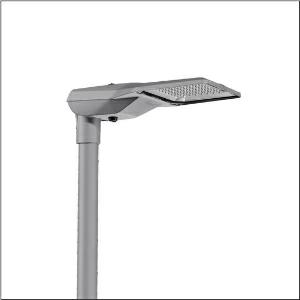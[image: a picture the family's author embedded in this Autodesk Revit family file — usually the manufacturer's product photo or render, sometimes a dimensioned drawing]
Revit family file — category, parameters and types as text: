
# Revit family: streetlight_sl_21_iq_midi___st1_0a_5xe3d31y08nb_4ee3
name_source: partatom
category: Lighting Fixtures
units: mm (PartAtom-declared; Revit-internal decimal feet)

## family parameters
Cut with Voids When Loaded = No
Host = Face
Light Source = No
Part Type = Normal
Room Calculation Point = No
Round Connector Dimension = Use Diameter
Shared = No

## types (1)
- --- (1 x LED, 21550 lm, 136.6 W, 3000K)
    Apparent Load = 137 VA
    CIE Flux Codes = 40 73 97 100 100
    Color Rendering = 70
    Color Temperature = 3000K
    Default Elevation = 1800 mm
    Description = Streetlight SL 21 iQ midi, mast luminaire, primary light control with lens, of PMMA, primary optical cover: cover, of toughened safety glass, transparent, light distribution: ST1.0a, light emission: direct distribution, primary light characteristic: asymmetric, installation type: post-top, side-entry, LED, High Power LED, rated luminous flux: 21.550lm, luminous efficacy: 158lm/W, light colour: 730, colour temperature: 3000K, control: pre-setting: logarithmic dimming characteristic, Street-Remote, Auto-Match, Temp-Guard, Lumen-Switch, Night-Set, Smart-Wire, Light-Fading, Desk-Remote (wireless, voltage-free reading and setting of iQ features in the workshop via application-optimized NFC function/RFID function), optimised constant luminous flux control (CLO 2.0), mains connection: 230..240V, AC, 50/60Hz, start of lifetime: 137W, end of service life: 144W, reduction: 61W, luminaire housing, of diecast aluminium, powder-coated, Siteco® metallic grey (DB 702S), corrosivity category C5 mid according to DIN EN ISO 12944, please order mast flange separately, inclination adjustable: 0°, 5°, 10°, 15°, sealing non-destructively replaceable, multi-level sealing system, length: 644mm, width: 335mm, height: 110mm, mast flange for spigot size: 42mm (side-entry): 5XC10008XM4, 60/48mm (side-entry/post-top): 5XC10108XM2, 76/60mm (side-entry/post-top): 5XC10108XM1, Smart Interface below and above, protection rating (complete): IP66, insulation class (complete): insulation class II (safety insulation), certification: CE, ENEC, ENEC+, VDE, impact resistance: IK09, permissible operating ambient temperature for outdoor applications: -40..+50°C, standard-compliant lighting for roads and squares, packaging unit: 1 piece

Light Distribution: ST1.0a
    Height = 111 mm
    Lamp = 1 x LED
    Lamp Light Flux = 21550 lm
    Lamp Power = 136.6 W
    Lamp count = 1
    Length = 644 mm
    Luminous efficacy = 158 lm/W
    Manufacturer = Siteco
    ModVariant = No
    Model = 5XE3D31Y08NB
    Number of Poles = 1
    OnlyDefault = Yes
    Power Factor = 1
    Product Name = Streetlight SL 21 iQ midi | ST1.0a
    Product group = mast luminaire | pylon top
    ProductGroupID = 6100
    Protection Class = Protection class II
    Protection Degree = IP 66
    RLX_Detail_Level = 1
    RLX_Emergency_Light_Flux = 0 lm
    RLX_Emergency_Type = 0
    RLX_Emergency_Type_DB = No
    RlxData = <blob elided: 91177 chars, md5=5352693a>
    Socket = socket
    Standby Power = 0 W
    System Light Flux = 21550 lm
    System Power = 137 W
    Type Comments = factory setting: luminous flux: 100 % | dim-lin: 254 | 733 mA
    Type Image = l_1004304.jpg
    URL = http://relux.com
    VarID = @adj_082653
    Voltage = 0 V
    Weight = 0.00 kg
    Width = 336 mm

## geometry (parser evidence)
native form markers: Blend x4, Sweep x9
no freeform markers — native parametric forms only
